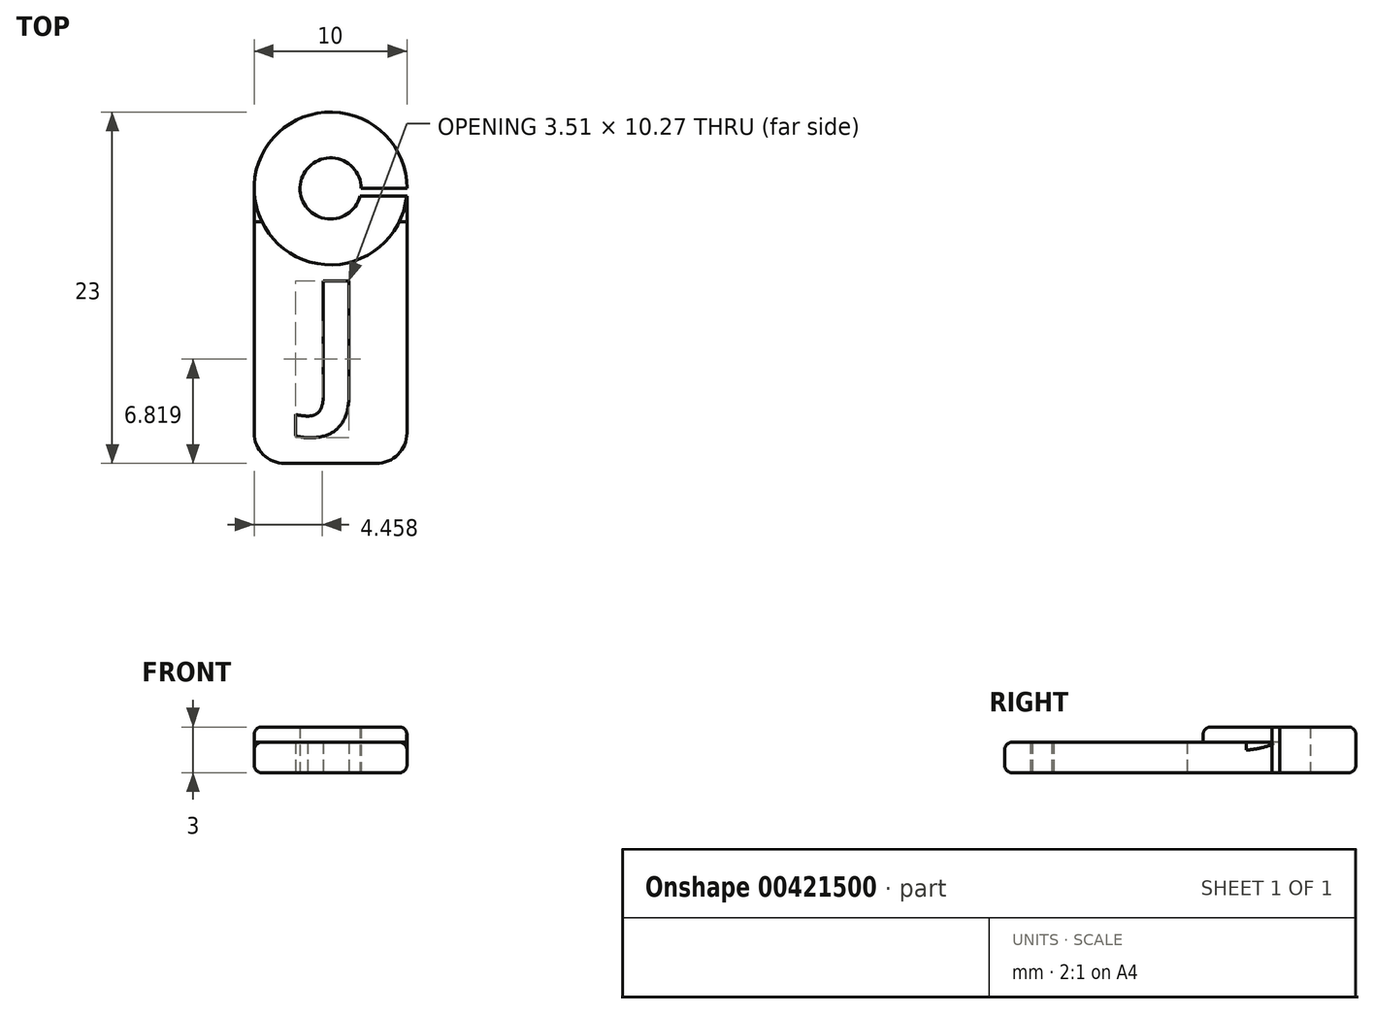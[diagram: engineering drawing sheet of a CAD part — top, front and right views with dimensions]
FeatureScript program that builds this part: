
annotation { "Feature Type Name" : "Feature", "Feature Type Description" : "" }
export const myFeature = defineFeature(function(context is Context, id is Id, definition is map)
    precondition{}
    {
        {
            var Q0;
            Q0=qCreatedBy(makeId("Top.planeOp"),FACE);
            var sketch = newSketch(context, id + "F0", { "sketchPlane" : qUnion([Q0])});
            skCircle(sketch, "E0", {"center": v(0, 0) * mm, "radius": 5 * mm});
            skCircle(sketch, "E1", {"center": v(0, 0) * mm, "radius": 2 * mm});
            skLineSegment(sketch, "E2", {"start": v(-5, 0) * mm, "end": v(-5, -18) * mm});
            skLineSegment(sketch, "E3", {"start": v(5, 0) * mm, "end": v(5, -18) * mm});
            skLineSegment(sketch, "E4", {"start": v(5, -18) * mm, "end": v(-5, -18) * mm});
            skText(sketch, "E5", { "text": "J", "fontName": "OpenSans-Bold.ttf"});
            skLineSegment(sketch, "E6", {"start": v(5, 0) * mm, "end": v(2, 0) * mm});
            skLineSegment(sketch, "E7", {"start": v(5, -0.5) * mm, "end": v(1.94, -0.5) * mm});
            const initialGuessF0  = {"E5": [-0.00147, -0.01398, 1, 0, 0.008]};
            skSetInitialGuess(sketch, initialGuessF0);
            skSolve(sketch);
        }
        {
            var Q0;
            {var subQ0=sQuery(id+"F0.wireOp",EDGE,"E6");Q0=makeQuery(id+"F0.imprint","IMPRINT",FACE,{"disambiguationData":[TD([[makeQuery(id+"F0.imprint","IMPRINT",EDGE,{"derivedFrom":subQ0}),-1.0]])]});}
            extrude(context, id + "F1", {"entities" : qUnion([Q0]), "depth" : 3 * mm, "offsetDistance" : 25 * mm});
        }
        {
            var Q0;
            {var subQ0=sQuery(id+"F0.wireOp",EDGE,"E2");Q0=makeQuery(id+"F0.imprint","IMPRINT",FACE,{"disambiguationData":[TD([[makeQuery(id+"F0.imprint","IMPRINT",EDGE,{"derivedFrom":subQ0}),1.0]])]});}
            extrude(context, id + "F2", {"entities" : qUnion([Q0]), "operationType" : NewBodyOperationType.ADD, "depth" : 2 * mm, "offsetDistance" : 25 * mm});
        }
        {
            var Q0;
            Q0=makeQuery(id+"F2.opExtrude","SWEPT_EDGE",EDGE,{"disambiguationData":[OSD([sQuery(id+"F0.wireOp",EDGE,"E2"),sQuery(id+"F0.wireOp",EDGE,"E4")])]});
            var Q1;
            Q1=makeQuery(id+"F2.opExtrude","SWEPT_EDGE",EDGE,{"disambiguationData":[OSD([sQuery(id+"F0.wireOp",EDGE,"E3"),sQuery(id+"F0.wireOp",EDGE,"E4")])]});
            fillet(context, id + "F3", {"entities" : qUnion([Q0, Q1]), "tangentPropagation" : true, "radius" : 2 * mm, "defaultsChanged" : false, "vertexSettings" : [], "allowEdgeOverflow" : false});
        }
        {
            var Q0;
            Q0=makeQuery(id+"F2.opExtrude","CAP_EDGE",EDGE,{"disambiguationData":[OSD([sQuery(id+"F0.wireOp",EDGE,"E3")])],"isStart":false});
            var Q1;
            Q1=makeQuery(id+"F1.opExtrude","CAP_EDGE",EDGE,{"disambiguationData":[OSD([sQuery(id+"F0.wireOp",EDGE,"E0")])],"isStart":false});
            var Q2;
            Q2=makeQuery(id+"F2.opExtrude","CAP_EDGE",EDGE,{"disambiguationData":[OSD([sQuery(id+"F0.wireOp",EDGE,"E3")])],"isStart":true});
            fillet(context, id + "F4", {"entities" : qUnion([Q0, Q1, Q2]), "tangentPropagation" : true, "radius" : 0.5 * mm, "defaultsChanged" : false, "vertexSettings" : [], "allowEdgeOverflow" : false});
        }
    });
